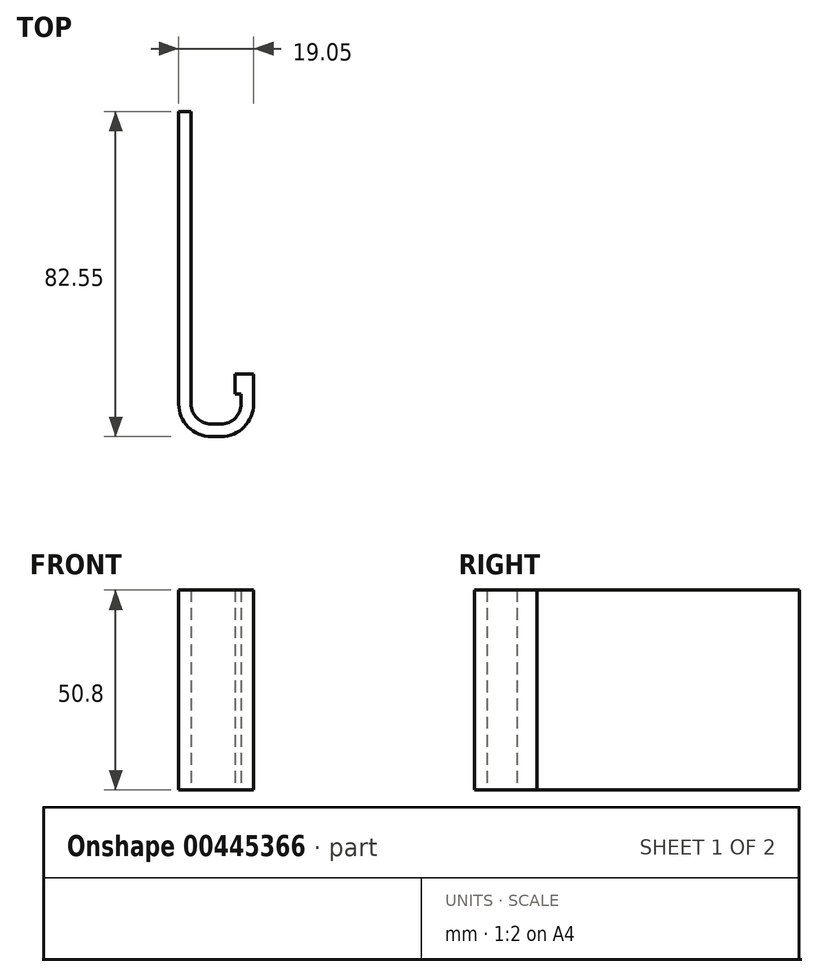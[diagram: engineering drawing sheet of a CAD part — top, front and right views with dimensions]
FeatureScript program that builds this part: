
annotation { "Feature Type Name" : "Feature", "Feature Type Description" : "" }
export const myFeature = defineFeature(function(context is Context, id is Id, definition is map)
    precondition{}
    {
        {
            var Q0;
            Q0=qCreatedBy(makeId("Top.planeOp"),FACE);
            var sketch = newSketch(context, id + "F0", { "sketchPlane" : qUnion([Q0])});
            skLineSegment(sketch, "E0", {"start": v(0, 0) * mm, "end": v(0, -74.3) * mm});
            skLineSegment(sketch, "E1", {"start": v(0, 0) * mm, "end": v(3.17, 0) * mm});
            skLineSegment(sketch, "E2", {"start": v(10.8, -82.55) * mm, "end": v(8.26, -82.55) * mm});
            skLineSegment(sketch, "E3.0", {"start": v(3.17, 0) * mm, "end": v(3.18, -74.3) * mm});
            skLineSegment(sketch, "E4.0", {"start": v(10.8, -79.38) * mm, "end": v(8.26, -79.38) * mm});
            skLineSegment(sketch, "E5.0", {"start": v(15.88, -66.68) * mm, "end": v(15.88, -74.3) * mm});
            skPoint(sketch, "E6.orphan", {"position": v(5.39, -82.55) * mm});
            skLineSegment(sketch, "E7.0", {"start": v(19.05, -66.68) * mm, "end": v(19.05, -74.3) * mm});
            skArc(sketch, "E8.filletArc", {"start": v(3.18, -74.3) * mm, "mid": v(4.66, -77.89) * mm, "end": v(8.26, -79.38) * mm});
            skArc(sketch, "E9.filletArc", {"start": v(10.8, -79.38) * mm, "mid": v(14.39, -77.89) * mm, "end": v(15.88, -74.3) * mm});
            skArc(sketch, "E10.0", {"start": v(10.8, -82.55) * mm, "mid": v(16.63, -80.13) * mm, "end": v(19.05, -74.3) * mm});
            skArc(sketch, "E11.0", {"start": v(0, -74.3) * mm, "mid": v(2.42, -80.13) * mm, "end": v(8.26, -82.55) * mm});
            skPoint(sketch, "E12.orphan", {"position": v(0, -82.55) * mm});
            skLineSegment(sketch, "E13.0", {"start": v(19.05, -66.68) * mm, "end": v(15.88, -66.68) * mm});
            skSolve(sketch);
        }
        {
            var Q0;
            Q0=makeQuery(id+"F0.imprint","IMPRINT",FACE,{"disambiguationData":[TD([[makeQuery(id+"F0.imprint","IMPRINT",EDGE,{"derivedFrom":sQuery(id+"F0.wireOp",EDGE,"E0")}),1.0]])]});
            extrude(context, id + "F1", {"entities" : qUnion([Q0]), "depth" : 50.8 * mm});
        }
        {
            var Q0;
            Q0=makeQuery(id+"F1.opExtrude","CAP_FACE",FACE,{"disambiguationData":[OSD([sQuery(id+"F0.wireOp",EDGE,"E0"),sQuery(id+"F0.wireOp",EDGE,"E1"),sQuery(id+"F0.wireOp",EDGE,"E2"),sQuery(id+"F0.wireOp",EDGE,"E3.0"),sQuery(id+"F0.wireOp",EDGE,"E4.0"),sQuery(id+"F0.wireOp",EDGE,"E5.0"),sQuery(id+"F0.wireOp",EDGE,"E7.0"),sQuery(id+"F0.wireOp",EDGE,"E8.filletArc"),sQuery(id+"F0.wireOp",EDGE,"E9.filletArc"),sQuery(id+"F0.wireOp",EDGE,"E10.0"),sQuery(id+"F0.wireOp",EDGE,"E11.0"),sQuery(id+"F0.wireOp",EDGE,"E13.0")])],"isStart":true});
            var sketch = newSketch(context, id + "F2", { "sketchPlane" : qUnion([Q0])});
            skLineSegment(sketch, "E14", {"start": v(15.88, 66.68) * mm, "end": v(14.35, 66.68) * mm});
            skLineSegment(sketch, "E15", {"start": v(14.35, 66.68) * mm, "end": v(14.35, 71.76) * mm});
            skLineSegment(sketch, "E16", {"start": v(14.35, 71.76) * mm, "end": v(15.88, 71.76) * mm});
            skLineSegment(sketch, "E17", {"start": v(15.88, 66.68) * mm, "end": v(15.88, 71.76) * mm});
            skSolve(sketch);
        }
        {
            var Q0;
            Q0=makeQuery(id+"F2.imprint","IMPRINT",FACE,{"disambiguationData":[TD([[makeQuery(id+"F2.imprint","IMPRINT",EDGE,{"derivedFrom":sQuery(id+"F2.wireOp",EDGE,"E14")}),-1.0]])]});
            extrude(context, id + "F3", {"entities" : qUnion([Q0]), "operationType" : NewBodyOperationType.ADD, "oppositeDirection" : true, "depth" : 50.8 * mm});
        }
    });
